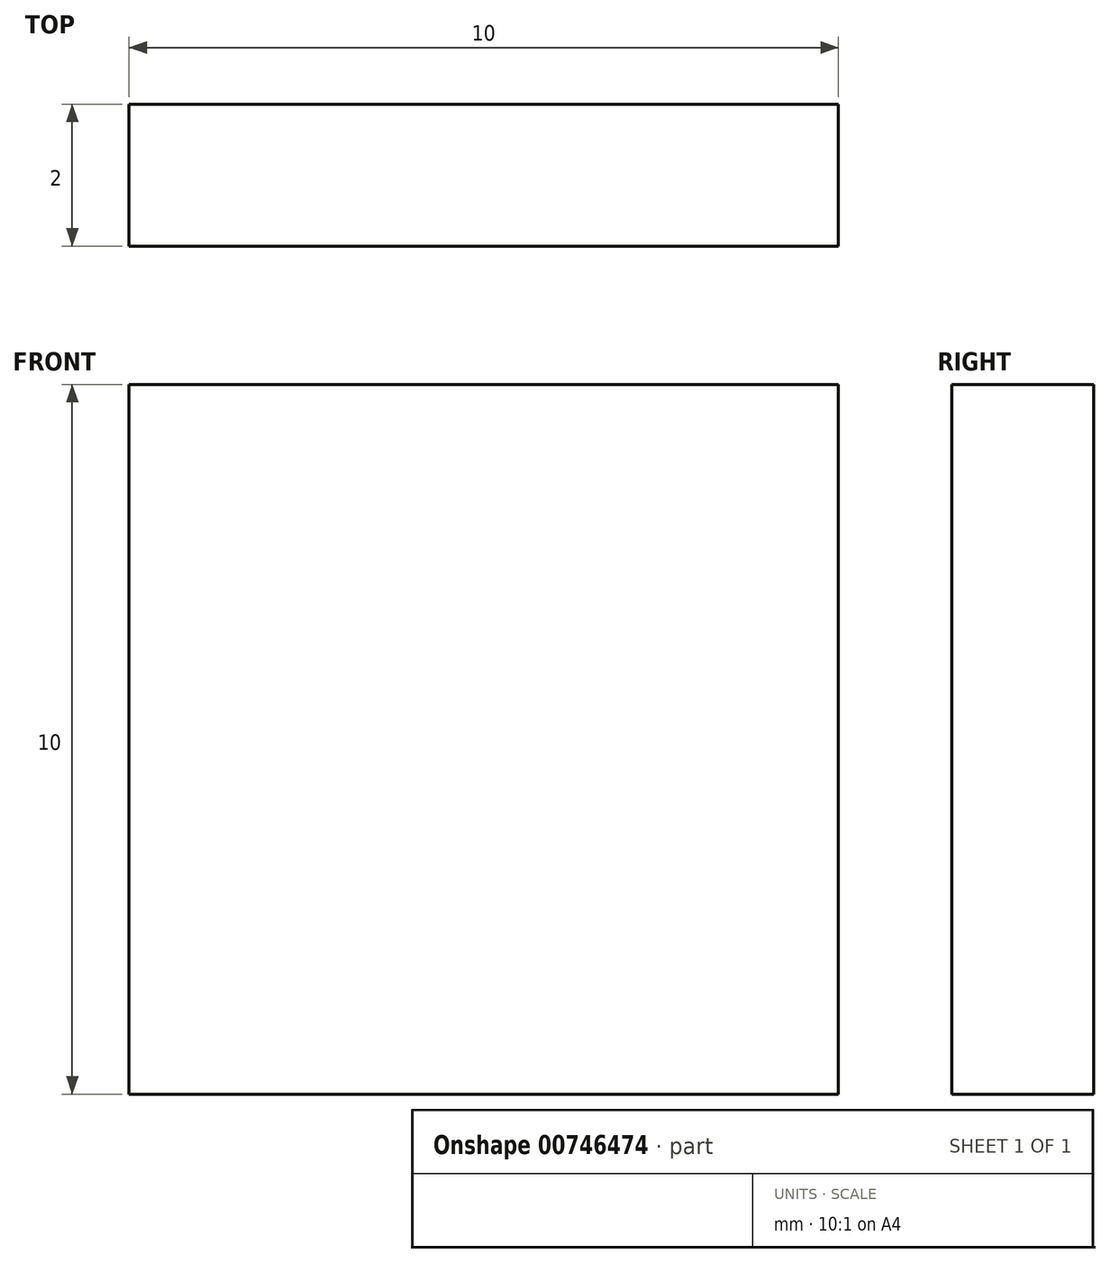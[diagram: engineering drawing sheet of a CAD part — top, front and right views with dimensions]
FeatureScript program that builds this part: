
annotation { "Feature Type Name" : "Feature", "Feature Type Description" : "" }
export const myFeature = defineFeature(function(context is Context, id is Id, definition is map)
    precondition{}
    {
        {
            var Q0;
            Q0=qCreatedBy(makeId("Front.planeOp"),FACE);
            var sketch = newSketch(context, id + "F0", { "sketchPlane" : qUnion([Q0])});
            skLineSegment(sketch, "E0.bottom", {"start": v(0, 0) * mm, "end": v(10, 0) * mm});
            skLineSegment(sketch, "E0.top", {"start": v(0, 10) * mm, "end": v(10, 10) * mm});
            skLineSegment(sketch, "E0.left", {"start": v(0, 0) * mm, "end": v(0, 10) * mm});
            skLineSegment(sketch, "E0.right", {"start": v(10, 0) * mm, "end": v(10, 10) * mm});
            skSolve(sketch);
        }
        {
            var Q0;
            Q0 = qSketchRegion(id + "F0", true);
            extrude(context, id + "F1", {"entities" : qUnion([Q0]), "depth" : 2 * mm, "offsetDistance" : 25 * mm});
        }
    });
